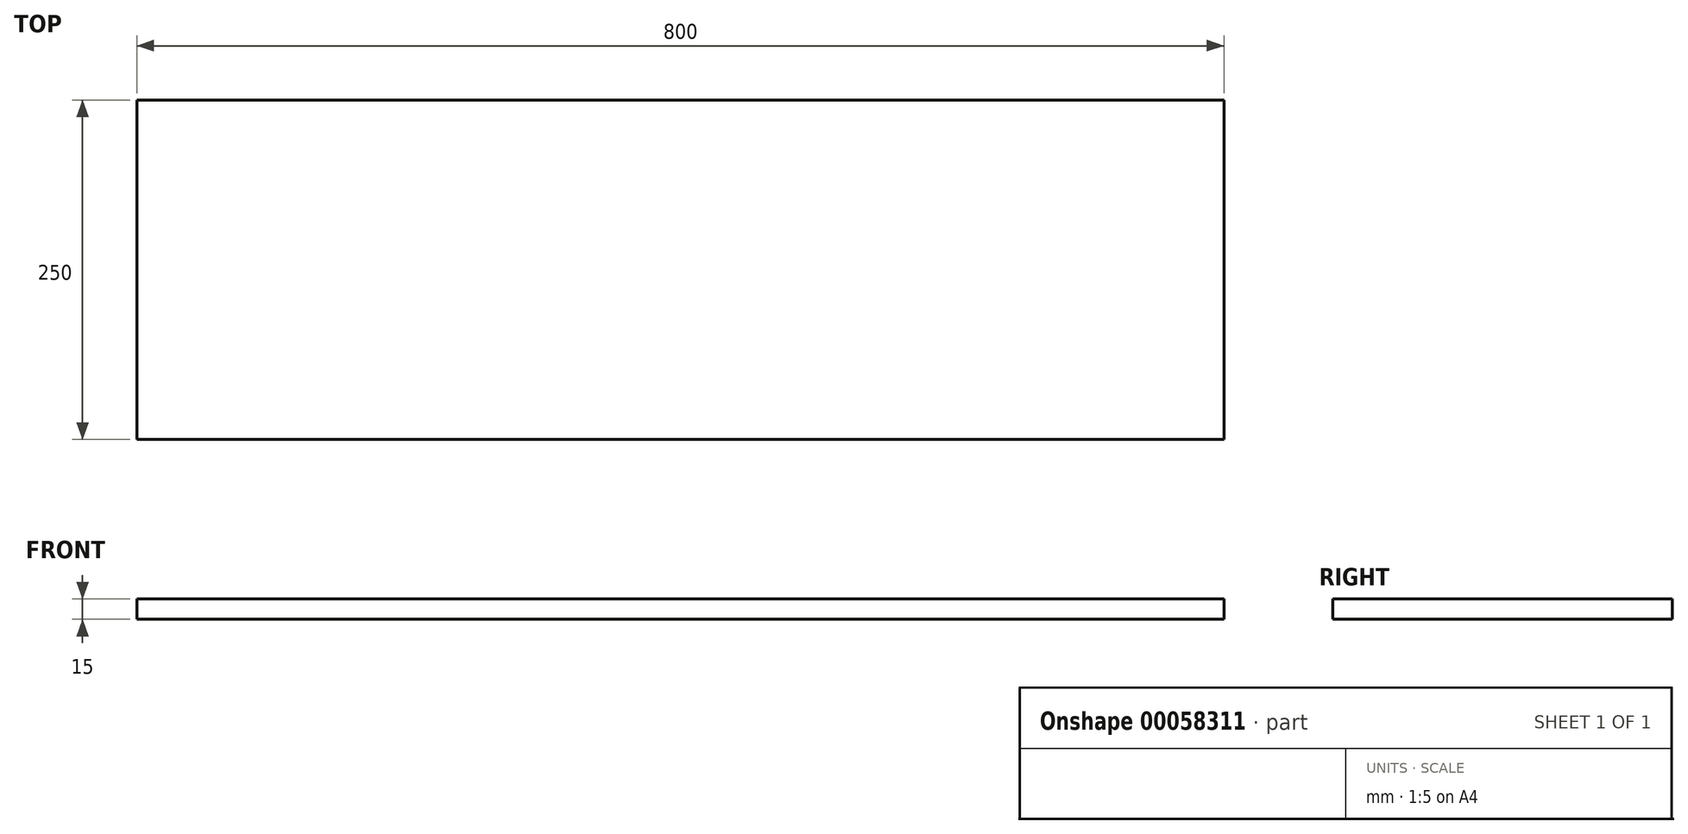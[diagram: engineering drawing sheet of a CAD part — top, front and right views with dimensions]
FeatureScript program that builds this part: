
annotation { "Feature Type Name" : "Feature", "Feature Type Description" : "" }
export const myFeature = defineFeature(function(context is Context, id is Id, definition is map)
    precondition{}
    {
        {
            var Q0;
            Q0=qCreatedBy(makeId("Top.planeOp"),FACE);
            var sketch = newSketch(context, id + "F0", { "sketchPlane" : qUnion([Q0])});
            skLineSegment(sketch, "E0.rect.bottom", {"start": v(400, -125) * mm, "end": v(-400, -125) * mm});
            skLineSegment(sketch, "E0.rect.top", {"start": v(400, 125) * mm, "end": v(-400, 125) * mm});
            skLineSegment(sketch, "E0.rect.left", {"start": v(400, -125) * mm, "end": v(400, 125) * mm});
            skLineSegment(sketch, "E0.rect.right", {"start": v(-400, -125) * mm, "end": v(-400, 125) * mm});
            skPoint(sketch, "E0.rect.middle", {"position": v(0, 0) * mm});
            skSolve(sketch);
        }
        {
            var Q0;
            Q0 = qSketchRegion(id + "F0", true);
            extrude(context, id + "F1", {"entities" : qUnion([Q0]), "depth" : 15 * mm});
        }
    });
